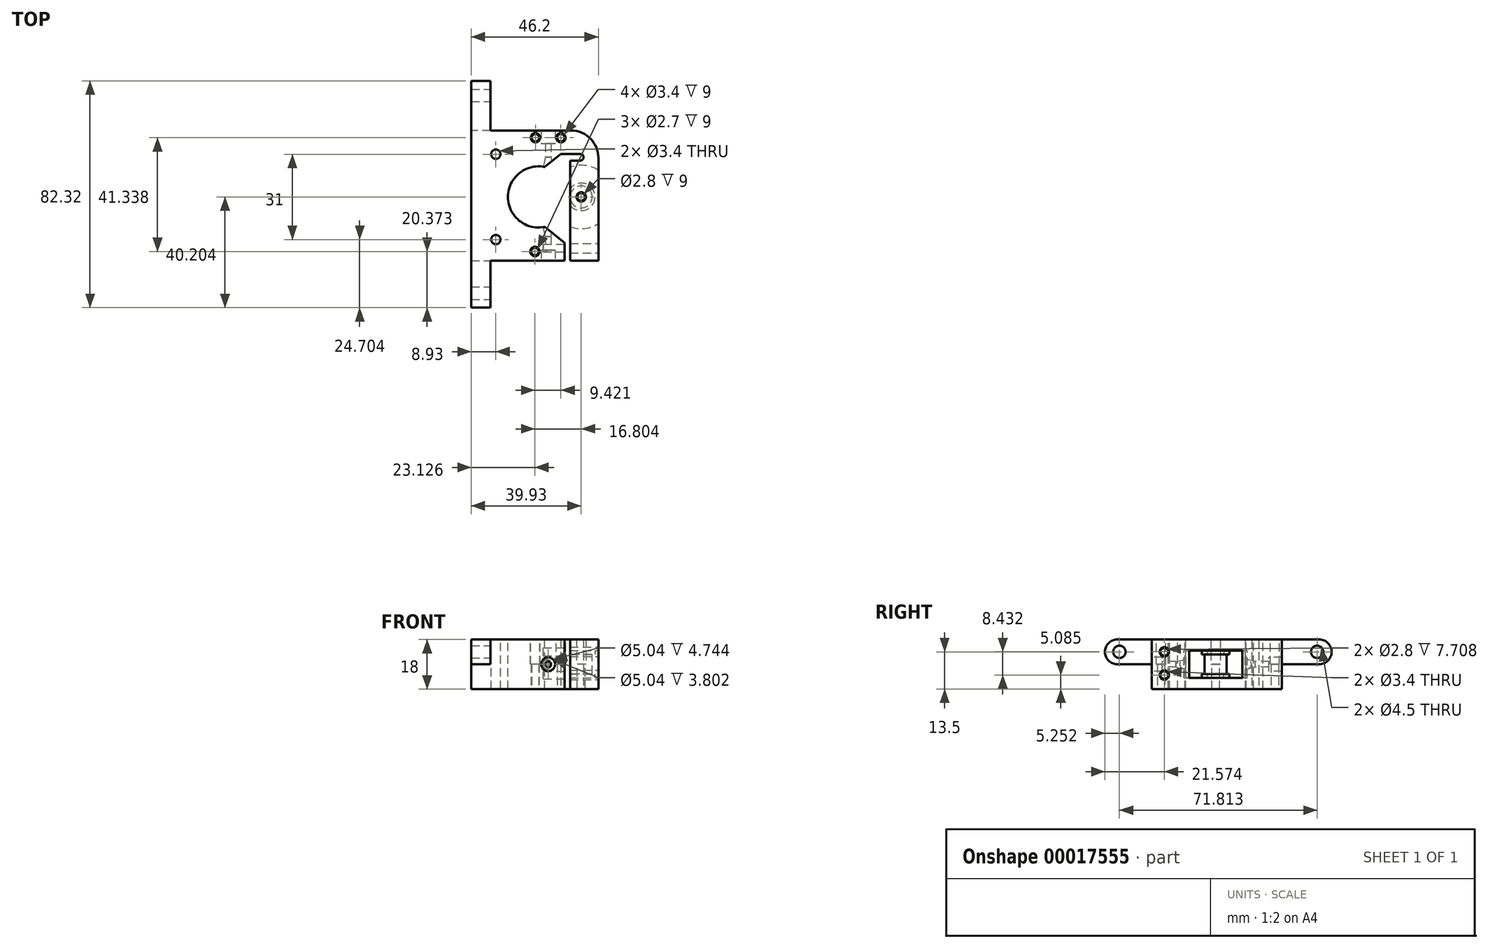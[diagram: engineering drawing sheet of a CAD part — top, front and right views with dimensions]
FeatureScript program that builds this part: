
annotation { "Feature Type Name" : "Feature", "Feature Type Description" : "" }
export const myFeature = defineFeature(function(context is Context, id is Id, definition is map)
    precondition{}
    {
        {
            var Q0;
            Q0=qCreatedBy(makeId("Top.planeOp"),FACE);
            var sketch = newSketch(context, id + "F0", { "sketchPlane" : qUnion([Q0])});
            skLineSegment(sketch, "E0", {"start": v(-24.43, 29.94) * mm, "end": v(-24.43, -17.36) * mm});
            skLineSegment(sketch, "E1", {"start": v(-24.43, -17.36) * mm, "end": v(-24.43, -17.36) * mm});
            skLineSegment(sketch, "E2", {"start": v(-24.43, -17.36) * mm, "end": v(-24.43, -17.35) * mm});
            skLineSegment(sketch, "E3", {"start": v(-24.43, -17.35) * mm, "end": v(9.48, -17.35) * mm});
            skLineSegment(sketch, "E4", {"start": v(9.48, -17.35) * mm, "end": v(9.48, 21.46) * mm});
            skLineSegment(sketch, "E5", {"start": v(9.48, 21.46) * mm, "end": v(15.14, 21.46) * mm});
            skLineSegment(sketch, "E6", {"start": v(15.14, 19) * mm, "end": v(11.48, 19) * mm});
            skLineSegment(sketch, "E7", {"start": v(11.48, 19) * mm, "end": v(11.48, -17.35) * mm});
            skLineSegment(sketch, "E8", {"start": v(11.48, -17.35) * mm, "end": v(21.77, -17.35) * mm});
            skLineSegment(sketch, "E9", {"start": v(21.77, -17.35) * mm, "end": v(21.77, 29.94) * mm});
            skLineSegment(sketch, "E10", {"start": v(21.77, 29.94) * mm, "end": v(-24.43, 29.94) * mm});
            skCircle(sketch, "E11", {"center": v(-1.11, 27.33) * mm, "radius": 1.35 * mm});
            skCircle(sketch, "E12", {"center": v(8.12, 27.33) * mm, "radius": 1.35 * mm});
            skCircle(sketch, "E13", {"center": v(-1.3, -14) * mm, "radius": 1.35 * mm});
            skArc(sketch, "E14", {"start": v(15.14, 19) * mm, "mid": v(16.36, 20.23) * mm, "end": v(15.14, 21.46) * mm});
            skCircle(sketch, "E15", {"center": v(-1.11, 27.33) * mm, "radius": 1.7 * mm});
            skCircle(sketch, "E16", {"center": v(8.12, 27.33) * mm, "radius": 1.7 * mm});
            skCircle(sketch, "E17", {"center": v(-1.3, -14) * mm, "radius": 1.7 * mm});
            skSolve(sketch);
        }
        {
            var Q0;
            Q0=makeQuery(id+"F0.imprint","IMPRINT",FACE,{"disambiguationData":[TD([[makeQuery(id+"F0.imprint","IMPRINT",EDGE,{"derivedFrom":sQuery(id+"F0.wireOp",EDGE,"E0")}),1.0]])]});
            var Q1;
            Q1=makeQuery(id+"F0.imprint","IMPRINT",FACE,{"disambiguationData":[TD([[makeQuery(id+"F0.imprint","IMPRINT",EDGE,{"derivedFrom":sQuery(id+"F0.wireOp",EDGE,"E11")}),-1.0]])]});
            var Q2;
            Q2=makeQuery(id+"F0.imprint","IMPRINT",FACE,{"disambiguationData":[TD([[makeQuery(id+"F0.imprint","IMPRINT",EDGE,{"derivedFrom":sQuery(id+"F0.wireOp",EDGE,"E12")}),-1.0]])]});
            var Q3;
            Q3=makeQuery(id+"F0.imprint","IMPRINT",FACE,{"disambiguationData":[TD([[makeQuery(id+"F0.imprint","IMPRINT",EDGE,{"derivedFrom":sQuery(id+"F0.wireOp",EDGE,"E13")}),-1.0]])]});
            extrude(context, id + "F1", {"entities" : qUnion([Q0, Q1, Q2, Q3]), "depth" : 9 * mm});
        }
        {
            var Q0;
            Q0=makeQuery(id+"F1.opExtrude","CAP_FACE",FACE,{"disambiguationData":[OSD([sQuery(id+"F0.wireOp",EDGE,"E0"),sQuery(id+"F0.wireOp",EDGE,"E1"),sQuery(id+"F0.wireOp",EDGE,"E2"),sQuery(id+"F0.wireOp",EDGE,"E3"),sQuery(id+"F0.wireOp",EDGE,"E4"),sQuery(id+"F0.wireOp",EDGE,"E5"),sQuery(id+"F0.wireOp",EDGE,"E6"),sQuery(id+"F0.wireOp",EDGE,"E7"),sQuery(id+"F0.wireOp",EDGE,"E8"),sQuery(id+"F0.wireOp",EDGE,"E9"),sQuery(id+"F0.wireOp",EDGE,"E10"),sQuery(id+"F0.wireOp",EDGE,"604cad85-587a-4b7d-8070-06f4cba85480"),sQuery(id+"F0.wireOp",EDGE,"6e5e38c1-5bff-4efe-a8c5-b84022f0a049"),sQuery(id+"F0.wireOp",EDGE,"b8144507-9dd7-4af4-87a3-7b649dd00ae6"),sQuery(id+"F0.wireOp",EDGE,"b9c2cb7c-5e58-4995-888e-a78f0403fbb5"),sQuery(id+"F0.wireOp",EDGE,"885990ab-7576-4c23-8475-595d2769e284"),sQuery(id+"F0.wireOp",EDGE,"E11"),sQuery(id+"F0.wireOp",EDGE,"E12"),sQuery(id+"F0.wireOp",EDGE,"E13"),sQuery(id+"F0.wireOp",EDGE,"E14")])],"isStart":false});
            var sketch = newSketch(context, id + "F2", { "sketchPlane" : qUnion([Q0])});
            skCircle(sketch, "E18", {"center": v(0, 5.82) * mm, "radius": 11.1 * mm});
            skCircle(sketch, "E19", {"center": v(-15.5, 21.32) * mm, "radius": 1.7 * mm});
            skCircle(sketch, "E20", {"center": v(-15.5, -9.68) * mm, "radius": 1.7 * mm});
            skSolve(sketch);
        }
        {
            var Q0;
            Q0=qSketchRegion(id+"F2",true);
            extrude(context, id + "F3", {"entities" : qUnion([Q0]), "operationType" : NewBodyOperationType.REMOVE, "endBound" : BoundingType.THROUGH_ALL, "oppositeDirection" : true, "depth" : 25 * mm});
        }
        {
            var Q0;
            Q0=makeQuery(id+"F1.opExtrude","CAP_FACE",FACE,{"disambiguationData":[OSD([sQuery(id+"F0.wireOp",EDGE,"E0"),sQuery(id+"F0.wireOp",EDGE,"E1"),sQuery(id+"F0.wireOp",EDGE,"E2"),sQuery(id+"F0.wireOp",EDGE,"E3"),sQuery(id+"F0.wireOp",EDGE,"E4"),sQuery(id+"F0.wireOp",EDGE,"E5"),sQuery(id+"F0.wireOp",EDGE,"E6"),sQuery(id+"F0.wireOp",EDGE,"E7"),sQuery(id+"F0.wireOp",EDGE,"E8"),sQuery(id+"F0.wireOp",EDGE,"E9"),sQuery(id+"F0.wireOp",EDGE,"E10"),sQuery(id+"F0.wireOp",EDGE,"604cad85-587a-4b7d-8070-06f4cba85480"),sQuery(id+"F0.wireOp",EDGE,"6e5e38c1-5bff-4efe-a8c5-b84022f0a049"),sQuery(id+"F0.wireOp",EDGE,"E11"),sQuery(id+"F0.wireOp",EDGE,"E12"),sQuery(id+"F0.wireOp",EDGE,"E13"),sQuery(id+"F0.wireOp",EDGE,"E14")])],"isStart":false});
            var sketch = newSketch(context, id + "F4", { "sketchPlane" : qUnion([Q0])});
            skCircle(sketch, "E21", {"center": v(15.5, 5.82) * mm, "radius": 11.5 * mm});
            skCircle(sketch, "E22", {"center": v(15.5, 5.82) * mm, "radius": 5 * mm});
            skCircle(sketch, "E23", {"center": v(15.5, 5.82) * mm, "radius": 4 * mm});
            skLineSegment(sketch, "E24", {"start": v(0, 5.82) * mm, "end": v(31, 5.82) * mm, "construction": true});
            skCircle(sketch, "E25", {"center": v(15.5, 5.82) * mm, "radius": 1.4 * mm});
            skCircle(sketch, "E26", {"center": v(15.5, 5.82) * mm, "radius": 1.7 * mm});
            skSolve(sketch);
        }
        {
            var Q0;
            Q0=makeQuery(id+"F4.imprint","IMPRINT",FACE,{"disambiguationData":[TD([[makeQuery(id+"F4.imprint","IMPRINT",EDGE,{"derivedFrom":sQuery(id+"F4.wireOp",EDGE,"E22")}),-1.0]])]});
            extrude(context, id + "F5", {"entities" : qUnion([Q0]), "operationType" : NewBodyOperationType.REMOVE, "oppositeDirection" : true, "depth" : 5 * mm});
        }
        {
            var Q0;
            Q0=makeQuery(id+"F4.imprint","IMPRINT",FACE,{"disambiguationData":[TD([[makeQuery(id+"F4.imprint","IMPRINT",EDGE,{"derivedFrom":sQuery(id+"F4.wireOp",EDGE,"E22")}),1.0]])]});
            var Q1;
            Q1=makeQuery(id+"F4.imprint","IMPRINT",FACE,{"disambiguationData":[TD([[makeQuery(id+"F4.imprint","IMPRINT",EDGE,{"derivedFrom":sQuery(id+"F4.wireOp",EDGE,"E23")}),-1.0]])]});
            extrude(context, id + "F6", {"entities" : qUnion([Q0, Q1]), "operationType" : NewBodyOperationType.REMOVE, "oppositeDirection" : true, "depth" : 3.5 * mm});
        }
        {
            var Q0;
            {var subQ0=sQuery(id+"F0.wireOp",EDGE,"E0");var subQ1=sQuery(id+"F0.wireOp",EDGE,"E1");var subQ2=sQuery(id+"F0.wireOp",EDGE,"E2");var subQ3=sQuery(id+"F0.wireOp",EDGE,"E3");var subQ4=sQuery(id+"F0.wireOp",EDGE,"E4");var subQ5=sQuery(id+"F0.wireOp",EDGE,"E5");var subQ6=sQuery(id+"F0.wireOp",EDGE,"E6");var subQ7=sQuery(id+"F0.wireOp",EDGE,"E7");var subQ8=sQuery(id+"F0.wireOp",EDGE,"E9");var subQ9=sQuery(id+"F0.wireOp",EDGE,"E10");var subQ10=sQuery(id+"F0.wireOp",EDGE,"604cad85-587a-4b7d-8070-06f4cba85480");var subQ11=sQuery(id+"F0.wireOp",EDGE,"6e5e38c1-5bff-4efe-a8c5-b84022f0a049");var subQ12=sQuery(id+"F0.wireOp",EDGE,"E11");var subQ13=sQuery(id+"F0.wireOp",EDGE,"E12");var subQ14=sQuery(id+"F0.wireOp",EDGE,"E13");var subQ15=sQuery(id+"F0.wireOp",EDGE,"E14");Q0=makeQuery(id+"F5.boolean.opBoolean","SPLIT",FACE,{"disambiguationData":[TD([makeQuery(id+"F1.opExtrude","SWEPT_FACE",FACE,{"disambiguationData":[OSD([subQ0])]})])],"derivedFrom":makeQuery(id+"F1.opExtrude","CAP_FACE",FACE,{"disambiguationData":[OSD([subQ0,subQ1,subQ2,subQ3,subQ4,subQ5,subQ6,subQ7,sQuery(id+"F0.wireOp",EDGE,"E8"),subQ8,subQ9,subQ10,subQ11,subQ12,subQ13,subQ14,subQ15])],"isStart":false})});}
            var sketch = newSketch(context, id + "F7", { "sketchPlane" : qUnion([Q0])});
            skLineSegment(sketch, "E27", {"start": v(0.98, 30.2) * mm, "end": v(0.98, 25.2) * mm});
            skLineSegment(sketch, "E28", {"start": v(0.98, 25.2) * mm, "end": v(2.5, 25.2) * mm});
            skLineSegment(sketch, "E29", {"start": v(2.5, 25.2) * mm, "end": v(2.5, 20.21) * mm});
            skLineSegment(sketch, "E30", {"start": v(2.5, 20.21) * mm, "end": v(1.31, 15.18) * mm});
            skLineSegment(sketch, "E31", {"start": v(1.31, 15.18) * mm, "end": v(3.5, 15.18) * mm});
            skLineSegment(sketch, "E32", {"start": v(3.5, 15.18) * mm, "end": v(3.5, 30.2) * mm});
            skLineSegment(sketch, "E33", {"start": v(3.5, 30.2) * mm, "end": v(0.98, 30.2) * mm});
            skLineSegment(sketch, "E34", {"start": v(0, 5.82) * mm, "end": v(31.4, 5.82) * mm, "construction": true});
            skLineSegment(sketch, "E35.0.MirrorCS", {"start": v(0.98, -13.54) * mm, "end": v(2.5, -13.54) * mm});
            skLineSegment(sketch, "E35.1.MirrorCS", {"start": v(3.5, -3.53) * mm, "end": v(3.5, -18.54) * mm});
            skLineSegment(sketch, "E35.2.MirrorCS", {"start": v(0.98, -18.54) * mm, "end": v(0.98, -13.54) * mm});
            skLineSegment(sketch, "E35.3.MirrorCS", {"start": v(1.31, -3.53) * mm, "end": v(3.5, -3.53) * mm});
            skLineSegment(sketch, "E35.4.MirrorCS", {"start": v(2.5, -8.56) * mm, "end": v(1.31, -3.53) * mm});
            skLineSegment(sketch, "E35.5.MirrorCS", {"start": v(2.5, -13.54) * mm, "end": v(2.5, -8.56) * mm});
            skLineSegment(sketch, "E35.6.MirrorCS", {"start": v(3.5, -18.54) * mm, "end": v(0.98, -18.54) * mm});
            skSolve(sketch);
        }
        {
            var Q0;
            Q0=qSketchRegion(id+"F7",true);
            var Q1;
            Q1=sQuery(id+"F7.wireOp",EDGE,"E32");
            revolve(context, id + "F8", {"entities" : qUnion([Q0]), "axis" : qUnion([Q1]), "revolveType" : RevolveType.FULL});
        }
        {
            var Q0;
            Q0=makeQuery(id+"F8.opRevolve","SWEPT_BODY",BODY,{"disambiguationData":[OSD([sQuery(id+"F7.wireOp",EDGE,"E27"),sQuery(id+"F7.wireOp",EDGE,"E28"),sQuery(id+"F7.wireOp",EDGE,"E29"),sQuery(id+"F7.wireOp",EDGE,"E30"),sQuery(id+"F7.wireOp",EDGE,"E31"),sQuery(id+"F7.wireOp",EDGE,"E32"),sQuery(id+"F7.wireOp",EDGE,"E33")])]});
            var Q1;
            Q1=makeQuery(id+"F1.opExtrude","SWEPT_BODY",BODY,{"disambiguationData":[OSD([sQuery(id+"F0.wireOp",EDGE,"E0"),sQuery(id+"F0.wireOp",EDGE,"E1"),sQuery(id+"F0.wireOp",EDGE,"E2"),sQuery(id+"F0.wireOp",EDGE,"E3"),sQuery(id+"F0.wireOp",EDGE,"E4"),sQuery(id+"F0.wireOp",EDGE,"E5"),sQuery(id+"F0.wireOp",EDGE,"E6"),sQuery(id+"F0.wireOp",EDGE,"E7"),sQuery(id+"F0.wireOp",EDGE,"E8"),sQuery(id+"F0.wireOp",EDGE,"E9"),sQuery(id+"F0.wireOp",EDGE,"E10"),sQuery(id+"F0.wireOp",EDGE,"604cad85-587a-4b7d-8070-06f4cba85480"),sQuery(id+"F0.wireOp",EDGE,"6e5e38c1-5bff-4efe-a8c5-b84022f0a049"),sQuery(id+"F0.wireOp",EDGE,"E11"),sQuery(id+"F0.wireOp",EDGE,"E12"),sQuery(id+"F0.wireOp",EDGE,"E13"),sQuery(id+"F0.wireOp",EDGE,"E14")])]});
            booleanBodies(context, id + "F9", {"operationType" : BooleanOperationType.SUBTRACTION, "tools" : qUnion([Q0]), "targets" : qUnion([Q1]), "keepTools" : true});
        }
        {
            var Q0;
            Q0=makeQuery(id+"F8.opRevolve","SWEPT_BODY",BODY,{"disambiguationData":[OSD([sQuery(id+"F7.wireOp",EDGE,"E35.0.MirrorCS"),sQuery(id+"F7.wireOp",EDGE,"E35.1.MirrorCS"),sQuery(id+"F7.wireOp",EDGE,"E35.2.MirrorCS"),sQuery(id+"F7.wireOp",EDGE,"E35.3.MirrorCS"),sQuery(id+"F7.wireOp",EDGE,"E35.4.MirrorCS"),sQuery(id+"F7.wireOp",EDGE,"E35.5.MirrorCS"),sQuery(id+"F7.wireOp",EDGE,"E35.6.MirrorCS")])]});
            var Q1;
            Q1=makeQuery(id+"F1.opExtrude","SWEPT_BODY",BODY,{"disambiguationData":[OSD([sQuery(id+"F0.wireOp",EDGE,"E0"),sQuery(id+"F0.wireOp",EDGE,"E1"),sQuery(id+"F0.wireOp",EDGE,"E2"),sQuery(id+"F0.wireOp",EDGE,"E3"),sQuery(id+"F0.wireOp",EDGE,"E4"),sQuery(id+"F0.wireOp",EDGE,"E5"),sQuery(id+"F0.wireOp",EDGE,"E6"),sQuery(id+"F0.wireOp",EDGE,"E7"),sQuery(id+"F0.wireOp",EDGE,"E8"),sQuery(id+"F0.wireOp",EDGE,"E9"),sQuery(id+"F0.wireOp",EDGE,"E10"),sQuery(id+"F0.wireOp",EDGE,"604cad85-587a-4b7d-8070-06f4cba85480"),sQuery(id+"F0.wireOp",EDGE,"6e5e38c1-5bff-4efe-a8c5-b84022f0a049"),sQuery(id+"F0.wireOp",EDGE,"E11"),sQuery(id+"F0.wireOp",EDGE,"E12"),sQuery(id+"F0.wireOp",EDGE,"E13"),sQuery(id+"F0.wireOp",EDGE,"E14")])]});
            booleanBodies(context, id + "F10", {"operationType" : BooleanOperationType.SUBTRACTION, "tools" : qUnion([Q0]), "targets" : qUnion([Q1]), "keepTools" : true});
        }
        {
            var Q0;
            Q0=makeQuery(id+"F1.opExtrude","SWEPT_EDGE",EDGE,{"disambiguationData":[OSD([sQuery(id+"F0.wireOp",EDGE,"E9"),sQuery(id+"F0.wireOp",EDGE,"E10")])]});
            fillet(context, id + "F11", {"entities" : qUnion([Q0]), "radius" : 10 * mm, "tangentPropagation" : true, "allowEdgeOverflow" : false});
        }
        {
            var Q0;
            Q0=qSketchRegion(id+"F0",true);
            extrude(context, id + "F12", {"entities" : qUnion([Q0]), "oppositeDirection" : true, "depth" : 9 * mm});
        }
        {
            var Q0;
            Q0=makeQuery(id+"F12.opExtrude","SWEPT_BODY",BODY,{"disambiguationData":[OSD([sQuery(id+"F0.wireOp",EDGE,"E0"),sQuery(id+"F0.wireOp",EDGE,"E3"),sQuery(id+"F0.wireOp",EDGE,"E4"),sQuery(id+"F0.wireOp",EDGE,"E5"),sQuery(id+"F0.wireOp",EDGE,"E6"),sQuery(id+"F0.wireOp",EDGE,"E7"),sQuery(id+"F0.wireOp",EDGE,"E8"),sQuery(id+"F0.wireOp",EDGE,"E9"),sQuery(id+"F0.wireOp",EDGE,"E10"),sQuery(id+"F0.wireOp",EDGE,"E11"),sQuery(id+"F0.wireOp",EDGE,"E12"),sQuery(id+"F0.wireOp",EDGE,"E13"),sQuery(id+"F0.wireOp",EDGE,"E14")])]});
            transform(context, id + "F13", {"entities" : qUnion([Q0]), "transformType" : TransformType.TRANSLATION_3D, "dx" : 0 * mm, "dy" : 0 * mm, "dz" : 18 * mm, "makeCopy" : false});
        }
        {
            var Q0;
            Q0=makeQuery(id+"F12.opExtrude","SWEPT_EDGE",EDGE,{"disambiguationData":[OSD([sQuery(id+"F0.wireOp",EDGE,"E9"),sQuery(id+"F0.wireOp",EDGE,"E10")])]});
            fillet(context, id + "F14", {"entities" : qUnion([Q0]), "radius" : 10 * mm, "tangentPropagation" : true, "allowEdgeOverflow" : false});
        }
        {
            var Q0;
            Q0=qSketchRegion(id+"F2",true);
            extrude(context, id + "F15", {"entities" : qUnion([Q0]), "operationType" : NewBodyOperationType.REMOVE, "endBound" : BoundingType.THROUGH_ALL, "depth" : 25 * mm});
        }
        {
            var Q0;
            {var subQ3=sQuery(id+"F4.wireOp",EDGE,"E21");var subQ7=makeQuery(id+"F1.opExtrude","CAP_EDGE",EDGE,{"disambiguationData":[OSD([sQuery(id+"F0.wireOp",EDGE,"E9")])],"isStart":false});var subQ9=makeQuery(id+"F4.imprint","INTERSECT",VERTEX,{"disambiguationData":[OD(0.0)],"derivedFrom":[subQ7,subQ3]});Q0=makeQuery(id+"F4.imprint","IMPRINT",FACE,{"disambiguationData":[TD([[makeQuery(id+"F4.imprint","IMPRINT",EDGE,{"disambiguationData":[TD([[subQ9,-1.0]])],"derivedFrom":subQ3}),1.0]])]});}
            extrude(context, id + "F16", {"entities" : qUnion([Q0]), "operationType" : NewBodyOperationType.REMOVE, "depth" : 5 * mm});
        }
        {
            var Q0;
            Q0=makeQuery(id+"F4.imprint","IMPRINT",FACE,{"disambiguationData":[TD([[makeQuery(id+"F4.imprint","IMPRINT",EDGE,{"derivedFrom":sQuery(id+"F4.wireOp",EDGE,"E23")}),-1.0]])]});
            extrude(context, id + "F17", {"entities" : qUnion([Q0]), "operationType" : NewBodyOperationType.REMOVE, "depth" : 3.5 * mm});
        }
        {
            var Q0;
            Q0=makeQuery(id+"F8.opRevolve","SWEPT_BODY",BODY,{"disambiguationData":[OSD([sQuery(id+"F7.wireOp",EDGE,"E27"),sQuery(id+"F7.wireOp",EDGE,"E28"),sQuery(id+"F7.wireOp",EDGE,"E29"),sQuery(id+"F7.wireOp",EDGE,"E30"),sQuery(id+"F7.wireOp",EDGE,"E31"),sQuery(id+"F7.wireOp",EDGE,"E32"),sQuery(id+"F7.wireOp",EDGE,"E33")])]});
            var Q1;
            Q1=makeQuery(id+"F12.opExtrude","SWEPT_BODY",BODY,{"disambiguationData":[OSD([sQuery(id+"F0.wireOp",EDGE,"E0"),sQuery(id+"F0.wireOp",EDGE,"E3"),sQuery(id+"F0.wireOp",EDGE,"E4"),sQuery(id+"F0.wireOp",EDGE,"E5"),sQuery(id+"F0.wireOp",EDGE,"E6"),sQuery(id+"F0.wireOp",EDGE,"E7"),sQuery(id+"F0.wireOp",EDGE,"E8"),sQuery(id+"F0.wireOp",EDGE,"E9"),sQuery(id+"F0.wireOp",EDGE,"E10"),sQuery(id+"F0.wireOp",EDGE,"E11"),sQuery(id+"F0.wireOp",EDGE,"E12"),sQuery(id+"F0.wireOp",EDGE,"E13"),sQuery(id+"F0.wireOp",EDGE,"E14")])]});
            booleanBodies(context, id + "F18", {"operationType" : BooleanOperationType.SUBTRACTION, "tools" : qUnion([Q0]), "targets" : qUnion([Q1])});
        }
        {
            var Q0;
            Q0=makeQuery(id+"F8.opRevolve","SWEPT_BODY",BODY,{"disambiguationData":[OSD([sQuery(id+"F7.wireOp",EDGE,"E35.0.MirrorCS"),sQuery(id+"F7.wireOp",EDGE,"E35.1.MirrorCS"),sQuery(id+"F7.wireOp",EDGE,"E35.2.MirrorCS"),sQuery(id+"F7.wireOp",EDGE,"E35.3.MirrorCS"),sQuery(id+"F7.wireOp",EDGE,"E35.4.MirrorCS"),sQuery(id+"F7.wireOp",EDGE,"E35.5.MirrorCS"),sQuery(id+"F7.wireOp",EDGE,"E35.6.MirrorCS")])]});
            var Q1;
            Q1=makeQuery(id+"F12.opExtrude","SWEPT_BODY",BODY,{"disambiguationData":[OSD([sQuery(id+"F0.wireOp",EDGE,"E0"),sQuery(id+"F0.wireOp",EDGE,"E3"),sQuery(id+"F0.wireOp",EDGE,"E4"),sQuery(id+"F0.wireOp",EDGE,"E5"),sQuery(id+"F0.wireOp",EDGE,"E6"),sQuery(id+"F0.wireOp",EDGE,"E7"),sQuery(id+"F0.wireOp",EDGE,"E8"),sQuery(id+"F0.wireOp",EDGE,"E9"),sQuery(id+"F0.wireOp",EDGE,"E10"),sQuery(id+"F0.wireOp",EDGE,"E11"),sQuery(id+"F0.wireOp",EDGE,"E12"),sQuery(id+"F0.wireOp",EDGE,"E13"),sQuery(id+"F0.wireOp",EDGE,"E14")])]});
            booleanBodies(context, id + "F19", {"operationType" : BooleanOperationType.SUBTRACTION, "tools" : qUnion([Q0]), "targets" : qUnion([Q1])});
        }
        {
            var Q0;
            Q0=makeQuery(id+"F12.opExtrude","SWEPT_FACE",FACE,{"disambiguationData":[OSD([sQuery(id+"F0.wireOp",EDGE,"E9")])]});
            var sketch = newSketch(context, id + "F20", { "sketchPlane" : qUnion([Q0])});
            skCircle(sketch, "E36", {"center": v(-12.8, 13.52) * mm, "radius": 1.7 * mm});
            skCircle(sketch, "E37", {"center": v(-12.8, 13.52) * mm, "radius": 1.4 * mm});
            skCircle(sketch, "E38", {"center": v(-12.8, 5.09) * mm, "radius": 1.7 * mm});
            skCircle(sketch, "E39", {"center": v(-12.8, 5.09) * mm, "radius": 1.4 * mm});
            skSolve(sketch);
        }
        {
            var Q0;
            Q0=makeQuery(id+"F20.imprint","IMPRINT",FACE,{"disambiguationData":[TD([[makeQuery(id+"F20.imprint","IMPRINT",EDGE,{"derivedFrom":sQuery(id+"F20.wireOp",EDGE,"E37")}),1.0]])]});
            extrude(context, id + "F21", {"entities" : qUnion([Q0]), "operationType" : NewBodyOperationType.REMOVE, "oppositeDirection" : true, "depth" : 20 * mm});
        }
        {
            var Q0;
            Q0=makeQuery(id+"F20.imprint","IMPRINT",FACE,{"disambiguationData":[TD([[makeQuery(id+"F20.imprint","IMPRINT",EDGE,{"derivedFrom":sQuery(id+"F20.wireOp",EDGE,"E36")}),1.0]])]});
            extrude(context, id + "F22", {"entities" : qUnion([Q0]), "operationType" : NewBodyOperationType.REMOVE, "oppositeDirection" : true, "depth" : 11 * mm});
        }
        {
            var Q0;
            Q0=makeQuery(id+"F20.imprint","IMPRINT",FACE,{"disambiguationData":[TD([[makeQuery(id+"F20.imprint","IMPRINT",EDGE,{"derivedFrom":sQuery(id+"F20.wireOp",EDGE,"E39")}),1.0]])]});
            extrude(context, id + "F23", {"entities" : qUnion([Q0]), "operationType" : NewBodyOperationType.REMOVE, "oppositeDirection" : true, "depth" : 20 * mm});
        }
        {
            var Q0;
            Q0=makeQuery(id+"F20.imprint","IMPRINT",FACE,{"disambiguationData":[TD([[makeQuery(id+"F20.imprint","IMPRINT",EDGE,{"derivedFrom":sQuery(id+"F20.wireOp",EDGE,"E38")}),1.0]])]});
            extrude(context, id + "F24", {"entities" : qUnion([Q0]), "operationType" : NewBodyOperationType.REMOVE, "oppositeDirection" : true, "depth" : 11 * mm});
        }
        {
            var Q0;
            Q0=makeQuery(id+"F4.imprint","IMPRINT",FACE,{"disambiguationData":[TD([[makeQuery(id+"F4.imprint","IMPRINT",EDGE,{"derivedFrom":sQuery(id+"F4.wireOp",EDGE,"E25")}),1.0]])]});
            extrude(context, id + "F25", {"entities" : qUnion([Q0]), "operationType" : NewBodyOperationType.REMOVE, "endBound" : BoundingType.THROUGH_ALL, "oppositeDirection" : true, "depth" : 25 * mm});
        }
        {
            var Q0;
            Q0=makeQuery(id+"F4.imprint","IMPRINT",FACE,{"disambiguationData":[TD([[makeQuery(id+"F4.imprint","IMPRINT",EDGE,{"derivedFrom":sQuery(id+"F4.wireOp",EDGE,"E25")}),1.0]])]});
            var Q1;
            Q1=makeQuery(id+"F4.imprint","IMPRINT",FACE,{"disambiguationData":[TD([[makeQuery(id+"F4.imprint","IMPRINT",EDGE,{"derivedFrom":sQuery(id+"F4.wireOp",EDGE,"E25")}),-1.0]])]});
            extrude(context, id + "F26", {"entities" : qUnion([Q0, Q1]), "operationType" : NewBodyOperationType.REMOVE, "endBound" : BoundingType.THROUGH_ALL, "depth" : 25 * mm});
        }
        {
            var Q0;
            Q0=makeQuery(id+"F12.opExtrude","SWEPT_FACE",FACE,{"disambiguationData":[OSD([sQuery(id+"F0.wireOp",EDGE,"E10")])]});
            var sketch = newSketch(context, id + "F27", { "sketchPlane" : qUnion([Q0])});
            skLineSegment(sketch, "E40.bottom", {"start": v(24.43, 9) * mm, "end": v(17.43, 9) * mm});
            skLineSegment(sketch, "E40.top", {"start": v(24.43, 18) * mm, "end": v(17.43, 18) * mm});
            skLineSegment(sketch, "E40.left", {"start": v(24.43, 9) * mm, "end": v(24.43, 18) * mm});
            skLineSegment(sketch, "E40.right", {"start": v(17.43, 9) * mm, "end": v(17.43, 18) * mm});
            skSolve(sketch);
        }
        {
            var Q0;
            Q0=qSketchRegion(id+"F27",true);
            extrude(context, id + "F28", {"entities" : qUnion([Q0]), "operationType" : NewBodyOperationType.ADD, "depth" : 18 * mm, "hasSecondDirection" : true, "secondDirectionOppositeDirection" : true, "secondDirectionDepth" : 64.31 * mm});
        }
        {
            var Q0;
            {var subQ0=sQuery(id+"F27.wireOp",EDGE,"E40.right");var subQ3=sQuery(id+"F0.wireOp",EDGE,"E3");Q0=makeQuery(id+"F28.boolean.opBoolean","SPLIT",FACE,{"disambiguationData":[TD([makeQuery(id+"F12.opExtrude","SWEPT_FACE",FACE,{"disambiguationData":[OSD([subQ3])]})])],"derivedFrom":makeQuery(id+"F28.opExtrude","SWEPT_FACE",FACE,{"disambiguationData":[OSD([subQ0])]})});}
            var sketch = newSketch(context, id + "F29", { "sketchPlane" : qUnion([Q0])});
            skCircle(sketch, "E41", {"center": v(-29.13, 13.5) * mm, "radius": 2.25 * mm});
            skPoint(sketch, "E42", {"position": v(-34.38, 13.5) * mm});
            skSolve(sketch);
        }
        {
            var Q0;
            {var subQ0=sQuery(id+"F27.wireOp",EDGE,"E40.right");var subQ3=sQuery(id+"F0.wireOp",EDGE,"E10");Q0=makeQuery(id+"F28.boolean.opBoolean","SPLIT",FACE,{"disambiguationData":[TD([makeQuery(id+"F12.opExtrude","SWEPT_FACE",FACE,{"disambiguationData":[OSD([subQ3])]})])],"derivedFrom":makeQuery(id+"F28.opExtrude","SWEPT_FACE",FACE,{"disambiguationData":[OSD([subQ0])]})});}
            var sketch = newSketch(context, id + "F30", { "sketchPlane" : qUnion([Q0])});
            skCircle(sketch, "E43", {"center": v(42.69, 13.5) * mm, "radius": 2.25 * mm});
            skPoint(sketch, "E44", {"position": v(47.94, 13.5) * mm});
            skSolve(sketch);
        }
        {
            var Q0;
            Q0=qSketchRegion(id+"F29",true);
            var Q1;
            Q1=qSketchRegion(id+"F30",true);
            extrude(context, id + "F31", {"entities" : qUnion([Q0, Q1]), "operationType" : NewBodyOperationType.REMOVE, "oppositeDirection" : true, "depth" : 25 * mm});
        }
        {
            var Q0;
            Q0=makeQuery(id+"F28.opExtrude","CAP_EDGE",EDGE,{"disambiguationData":[OSD([sQuery(id+"F27.wireOp",EDGE,"E40.top")])],"isStart":true});
            var Q1;
            Q1=makeQuery(id+"F28.opExtrude","CAP_EDGE",EDGE,{"disambiguationData":[OSD([sQuery(id+"F27.wireOp",EDGE,"E40.bottom")])],"isStart":true});
            var Q2;
            Q2=makeQuery(id+"F28.opExtrude","CAP_EDGE",EDGE,{"disambiguationData":[OSD([sQuery(id+"F27.wireOp",EDGE,"E40.top")])],"isStart":false});
            var Q3;
            Q3=makeQuery(id+"F28.opExtrude","CAP_EDGE",EDGE,{"disambiguationData":[OSD([sQuery(id+"F27.wireOp",EDGE,"E40.bottom")])],"isStart":false});
            fillet(context, id + "F32", {"entities" : qUnion([Q0, Q1, Q2, Q3]), "radius" : 4.5 * mm, "tangentPropagation" : true, "allowEdgeOverflow" : false});
        }
        {
            var Q0;
            Q0=makeQuery(id+"F3.boolean.opBoolean","INTERSECT",EDGE,{"disambiguationData":[OD(0.0)],"derivedFrom":[makeQuery(id+"F1.opExtrude","SWEPT_FACE",FACE,{"disambiguationData":[OSD([sQuery(id+"F0.wireOp",EDGE,"E4")])]}),makeQuery(id+"F3.opExtrude","SWEPT_FACE",FACE,{"disambiguationData":[OSD([sQuery(id+"F2.wireOp",EDGE,"E18")])]})]});
            var Q1;
            Q1=makeQuery(id+"F3.boolean.opBoolean","INTERSECT",EDGE,{"disambiguationData":[OD(1.0)],"derivedFrom":[makeQuery(id+"F1.opExtrude","SWEPT_FACE",FACE,{"disambiguationData":[OSD([sQuery(id+"F0.wireOp",EDGE,"E4")])]}),makeQuery(id+"F3.opExtrude","SWEPT_FACE",FACE,{"disambiguationData":[OSD([sQuery(id+"F2.wireOp",EDGE,"E18")])]})]});
            var Q2;
            Q2=makeQuery(id+"F15.boolean.opBoolean","INTERSECT",EDGE,{"disambiguationData":[OD(1.0)],"derivedFrom":[makeQuery(id+"F12.opExtrude","SWEPT_FACE",FACE,{"disambiguationData":[OSD([sQuery(id+"F0.wireOp",EDGE,"E4")])]}),makeQuery(id+"F15.opExtrude","SWEPT_FACE",FACE,{"disambiguationData":[OSD([sQuery(id+"F2.wireOp",EDGE,"E18")])]})]});
            var Q3;
            Q3=makeQuery(id+"F15.boolean.opBoolean","INTERSECT",EDGE,{"disambiguationData":[OD(0.0)],"derivedFrom":[makeQuery(id+"F12.opExtrude","SWEPT_FACE",FACE,{"disambiguationData":[OSD([sQuery(id+"F0.wireOp",EDGE,"E4")])]}),makeQuery(id+"F15.opExtrude","SWEPT_FACE",FACE,{"disambiguationData":[OSD([sQuery(id+"F2.wireOp",EDGE,"E18")])]})]});
            chamfer(context, id + "F33", {"entities" : qUnion([Q0, Q1, Q2, Q3]), "width" : 6 * mm, "tangentPropagation" : true});
        }
    });
